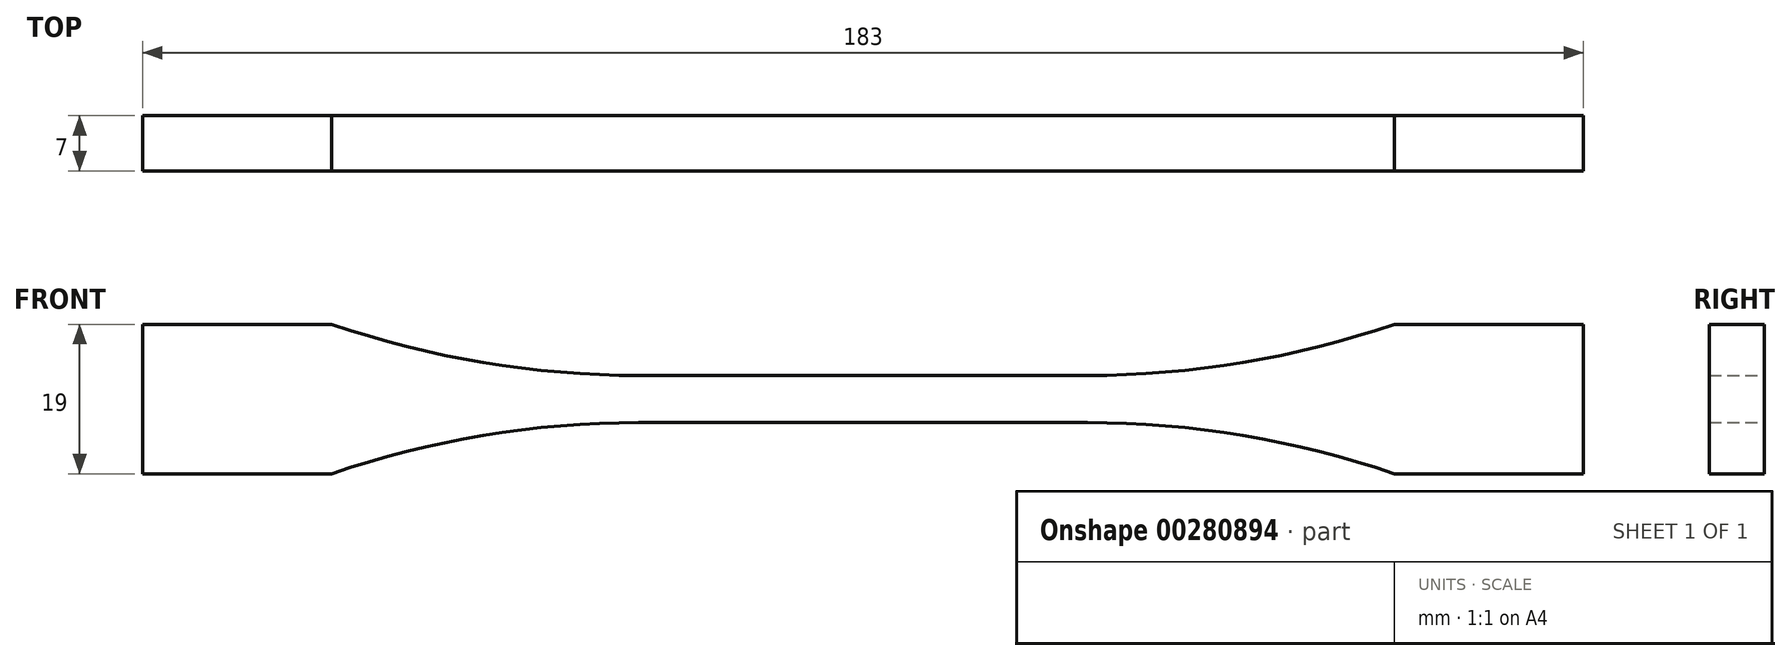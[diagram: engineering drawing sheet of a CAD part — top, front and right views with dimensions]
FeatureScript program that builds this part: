
annotation { "Feature Type Name" : "Feature", "Feature Type Description" : "" }
export const myFeature = defineFeature(function(context is Context, id is Id, definition is map)
    precondition{}
    {
        {
            var Q0;
            Q0=qCreatedBy(makeId("Front.planeOp"),FACE);
            var sketch = newSketch(context, id + "F0", { "sketchPlane" : qUnion([Q0])});
            skLineSegment(sketch, "E0", {"start": v(0, 3) * mm, "end": v(28.5, 3) * mm});
            skArc(sketch, "E1", {"start": v(28.5, 3) * mm, "mid": v(48.27, 4.64) * mm, "end": v(67.5, 9.5) * mm});
            skLineSegment(sketch, "E2", {"start": v(67.5, 9.5) * mm, "end": v(91.5, 9.5) * mm});
            skLineSegment(sketch, "E3.MirrorCS", {"start": v(67.5, -9.5) * mm, "end": v(91.5, -9.5) * mm});
            skLineSegment(sketch, "E4.MirrorCS", {"start": v(0, -3) * mm, "end": v(28.5, -3) * mm});
            skArc(sketch, "E5.MirrorCS", {"start": v(28.5, -3) * mm, "mid": v(48.27, -4.64) * mm, "end": v(67.5, -9.5) * mm});
            skArc(sketch, "E6.MirrorCS", {"start": v(-28.5, 3) * mm, "mid": v(-48.27, 4.64) * mm, "end": v(-67.5, 9.5) * mm});
            skLineSegment(sketch, "E7.MirrorCS", {"start": v(-67.5, 9.5) * mm, "end": v(-91.5, 9.5) * mm});
            skLineSegment(sketch, "E8.MirrorCS", {"start": v(-67.5, -9.5) * mm, "end": v(-91.5, -9.5) * mm});
            skLineSegment(sketch, "E9.MirrorCS", {"start": v(0, -3) * mm, "end": v(-28.5, -3) * mm});
            skLineSegment(sketch, "E10.MirrorCS", {"start": v(0, 3) * mm, "end": v(-28.5, 3) * mm});
            skArc(sketch, "E11.MirrorCS", {"start": v(-28.5, -3) * mm, "mid": v(-48.27, -4.64) * mm, "end": v(-67.5, -9.5) * mm});
            skLineSegment(sketch, "E12", {"start": v(-91.5, 9.5) * mm, "end": v(-91.5, -9.5) * mm});
            skLineSegment(sketch, "E13", {"start": v(91.5, 9.5) * mm, "end": v(91.5, -9.5) * mm});
            skSolve(sketch);
        }
        {
            var Q0;
            Q0 = qSketchRegion(id + "F0", true);
            extrude(context, id + "F1", {"entities" : qUnion([Q0]), "endBound" : BoundingType.SYMMETRIC, "depth" : 7 * mm});
        }
    });
